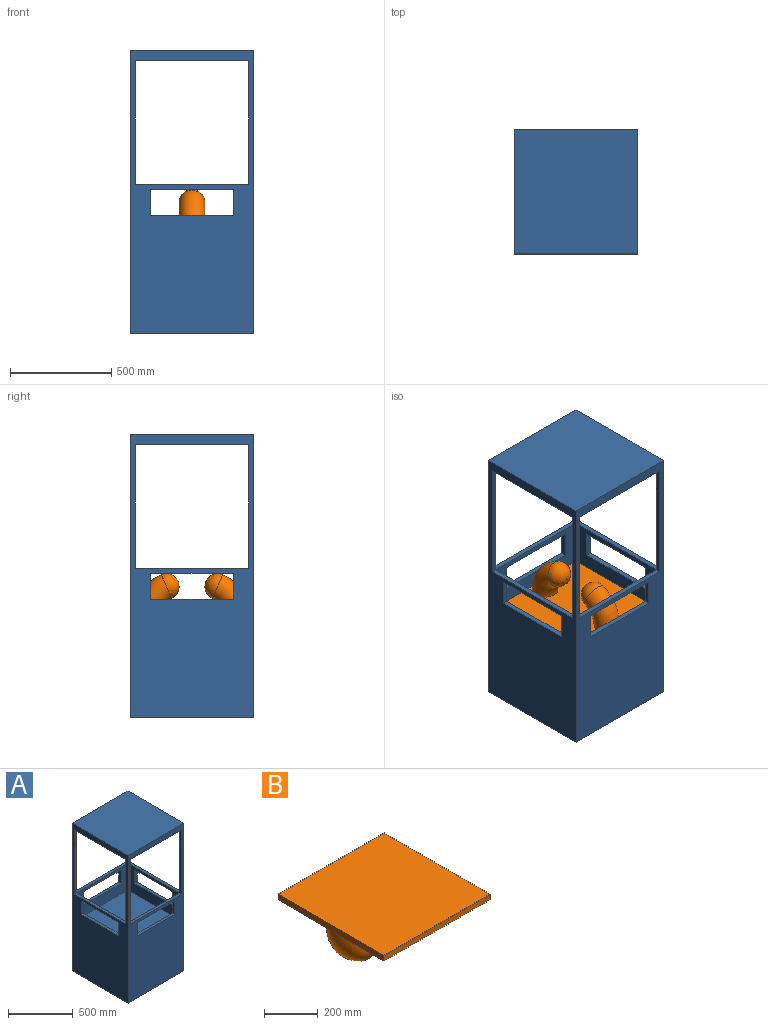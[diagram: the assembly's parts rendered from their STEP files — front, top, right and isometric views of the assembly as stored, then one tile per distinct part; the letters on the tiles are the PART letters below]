
ASSEMBLY  parts=2 mates=1
PART A: 45 faces, bbox 609.6x609.6x1397 mm
  f0: plane 1397x609.6mm, normal (1,0,0), area 459353.9mm2, adj f13,f14,f15,f21,f22,f33,f34,f35
  f1: plane 609.6x25.4mm, normal (1,0,0), area 15483.8mm2, adj f8,f15,f22,f32
  f2: plane 609.6x25.4mm, normal (1,0,0), area 15483.8mm2, adj f15,f19,f21,f30
  f3: plane 558.8x254mm, normal (1,0,0), area 90322.4mm2, adj f23,f24,f25,f26,f27,f28,f29,f31
  f4: plane 609.6x25.4mm, normal (-1,0,0), area 15483.8mm2, adj f8,f15,f22,f37
  f5: plane 609.6x25.4mm, normal (-1,0,0), area 15483.8mm2, adj f15,f19,f21,f39
  f6: plane 558.8x254mm, normal (-1,0,0), area 90322.4mm2, adj f23,f24,f25,f33,f34,f35,f36,f38
  f7: plane 1397x609.6mm, normal (-1,0,0), area 459353.9mm2, adj f13,f14,f15,f21,f22,f26,f27,f28
  f8: plane 558.8x25.4mm, normal (0,0,1), area 14193.5mm2, adj f1,f4,f22,f23
  f9: plane 127x25.4mm, normal (1,0,0), area 3225.8mm2, adj f10,f12,f22,f23
  f10: plane 406.4x25.4mm, normal (0,0,-1), area 10322.6mm2, adj f9,f11,f22,f23
  f11: plane 127x25.4mm, normal (-1,0,0), area 3225.8mm2, adj f10,f12,f22,f23
  f12: plane 406.4x25.4mm, normal (0,0,1), area 10322.6mm2, adj f9,f11,f22,f23
  f13: plane 609.6x609.6mm, normal (0,0,-1), area 59354.7mm2, adj f0,f7,f21,f22,f40,f41,f42,f43
  f14: plane 609.6x609.6mm, normal (0,0,1), area 371612.2mm2, adj f0,f7,f21,f22
  f15: plane 609.6x609.6mm, normal (0,0,-1), area 369031.5mm2, adj f0,f1,f2,f4,f5,f7,f21,f22
  f16: plane 127x25.4mm, normal (1,0,0), area 3225.8mm2, adj f17,f20,f21,f24
  f17: plane 406.4x25.4mm, normal (0,0,-1), area 10322.6mm2, adj f16,f18,f21,f24
  f18: plane 127x25.4mm, normal (-1,0,0), area 3225.8mm2, adj f17,f20,f21,f24
  f19: plane 558.8x25.4mm, normal (0,0,1), area 14193.5mm2, adj f2,f5,f21,f24
  f20: plane 406.4x25.4mm, normal (0,0,1), area 10322.6mm2, adj f16,f18,f21,f24
  f21: plane 1397x609.6mm, normal (0,-1,0), area 459353.9mm2, adj f0,f2,f5,f7,f13,f14,f15,f16
  f22: plane 1397x609.6mm, normal (0,1,0), area 459353.9mm2, adj f0,f1,f4,f7,f8,f9,f10,f11
  f23: plane 558.8x254mm, normal (0,-1,0), area 90322.4mm2, adj f3,f6,f8,f9,f10,f11,f12,f25
  f24: plane 558.8x254mm, normal (0,1,0), area 90322.4mm2, adj f3,f6,f16,f17,f18,f19,f20,f25
  f25: plane 558.8x558.8mm, normal (0,0,1), area 312257.4mm2, adj f3,f6,f23,f24
  f26: plane 127x25.4mm, normal (0,1,0), area 3225.8mm2, adj f3,f7,f27,f29
  f27: plane 406.4x25.4mm, normal (0,0,1), area 10322.6mm2, adj f3,f7,f26,f28
  f28: plane 127x25.4mm, normal (0,-1,0), area 3225.8mm2, adj f3,f7,f27,f29
  f29: plane 406.4x25.4mm, normal (0,0,-1), area 10322.6mm2, adj f3,f7,f26,f28
  f30: plane 609.6x25.4mm, normal (0,1,0), area 15483.8mm2, adj f2,f7,f15,f31
  f31: plane 558.8x25.4mm, normal (0,0,1), area 14193.5mm2, adj f3,f7,f30,f32
  f32: plane 609.6x25.4mm, normal (0,-1,0), area 15483.8mm2, adj f1,f7,f15,f31
  f33: plane 406.4x25.4mm, normal (0,0,-1), area 10322.6mm2, adj f0,f6,f34,f36
  f34: plane 127x25.4mm, normal (0,-1,0), area 3225.8mm2, adj f0,f6,f33,f35
  f35: plane 406.4x25.4mm, normal (0,0,1), area 10322.6mm2, adj f0,f6,f34,f36
  f36: plane 127x25.4mm, normal (0,1,0), area 3225.8mm2, adj f0,f6,f33,f35
  f37: plane 609.6x25.4mm, normal (0,-1,0), area 15483.8mm2, adj f0,f4,f15,f38
  f38: plane 558.8x25.4mm, normal (0,0,1), area 14193.5mm2, adj f0,f6,f37,f39
  f39: plane 609.6x25.4mm, normal (0,1,0), area 15483.8mm2, adj f0,f5,f15,f38
  f40: plane 558.8x457.2mm, normal (0,-1,0), area 255483.4mm2, adj f13,f41,f43,f44
  f41: plane 558.8x457.2mm, normal (-1,0,0), area 255483.4mm2, adj f13,f40,f42,f44
  f42: plane 558.8x457.2mm, normal (0,1,0), area 255483.4mm2, adj f13,f41,f43,f44
  f43: plane 558.8x457.2mm, normal (1,0,0), area 255483.4mm2, adj f13,f40,f42,f44
  f44: plane 558.8x558.8mm, normal (0,0,-1), area 312257.4mm2, adj f40,f41,f42,f43
PART B: 12 faces, bbox 594.4x558.8x261.5 mm
  f0: plane 558.8x25.4mm, normal (1,0,0), area 14193.5mm2, adj f1,f3,f4,f5
  f1: plane 558.8x25.4mm, normal (0,1,0), area 14193.5mm2, adj f0,f2,f4,f5
  f2: plane 558.8x25.4mm, normal (-1,0,0), area 14193.5mm2, adj f1,f3,f4,f5
  f3: plane 558.8x25.4mm, normal (0,-1,0), area 14193.5mm2, adj f0,f2,f4,f5
  f4: plane 558.8x558.8mm, normal (0,0,1), area 312257.4mm2, adj f0,f1,f2,f3
  f5: plane 558.8x558.8mm, normal (0,0,-1), area 286922.1mm2, adj f0,f1,f2,f3,f6,f8
  f6: torus R=152.4mm, axis (0,1,0), area 69982.1mm2, adj f5,f11
  f7: plane 2.78x2.54mm, normal (1,0,0), area 5.6mm2, adj f11
  f8: torus R=152.4mm, axis (0,-1,0), area 69982.1mm2, adj f5,f10
  f9: plane 2.78x2.54mm, normal (-1,0,0), area 5.5mm2, adj f10
  f10: bspline ~155.12x138.84mm, area 25098.5mm2, adj f8,f9
  f11: bspline ~155.12x138.84mm, area 25098.5mm2, adj f6,f7
PLACE A t=(123.77,19.73,41.58)mm
PLACE B rot(axis=(-0.71,-0.71,0),180deg) t=(123.77,19.73,-148.92)mm
MATE fastened B.f4 <-> A.f25  axis (0,0,-1) through (123.77,19.73,-174.32)mm
